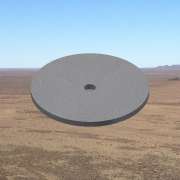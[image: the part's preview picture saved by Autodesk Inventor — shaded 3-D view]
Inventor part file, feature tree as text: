
AUTODESK INVENTOR PART (.ipt)
format: ipt  version: 2013 SP2 (Build 170200200, 200)  size: 142,336 bytes
history: native  units: in
note: dims shown in document units (in); Inventor stores cm internally (conversion verified against a paired STEP export)
features: extrude x1, sketch x1
ambient origin geometry x8: Origin, YZ Plane, XZ Plane, XY Plane, X Axis, Y Axis, Z Axis, Center Point
bodies: Solid1 (feature_tree)
feature tree (2):
  extrude  "Extrusion1"  Depth=1.0in
  sketch  "Sketch1"  dims[d0=10.0in d2=1.0in d3=0.5in d4=0.0in]
